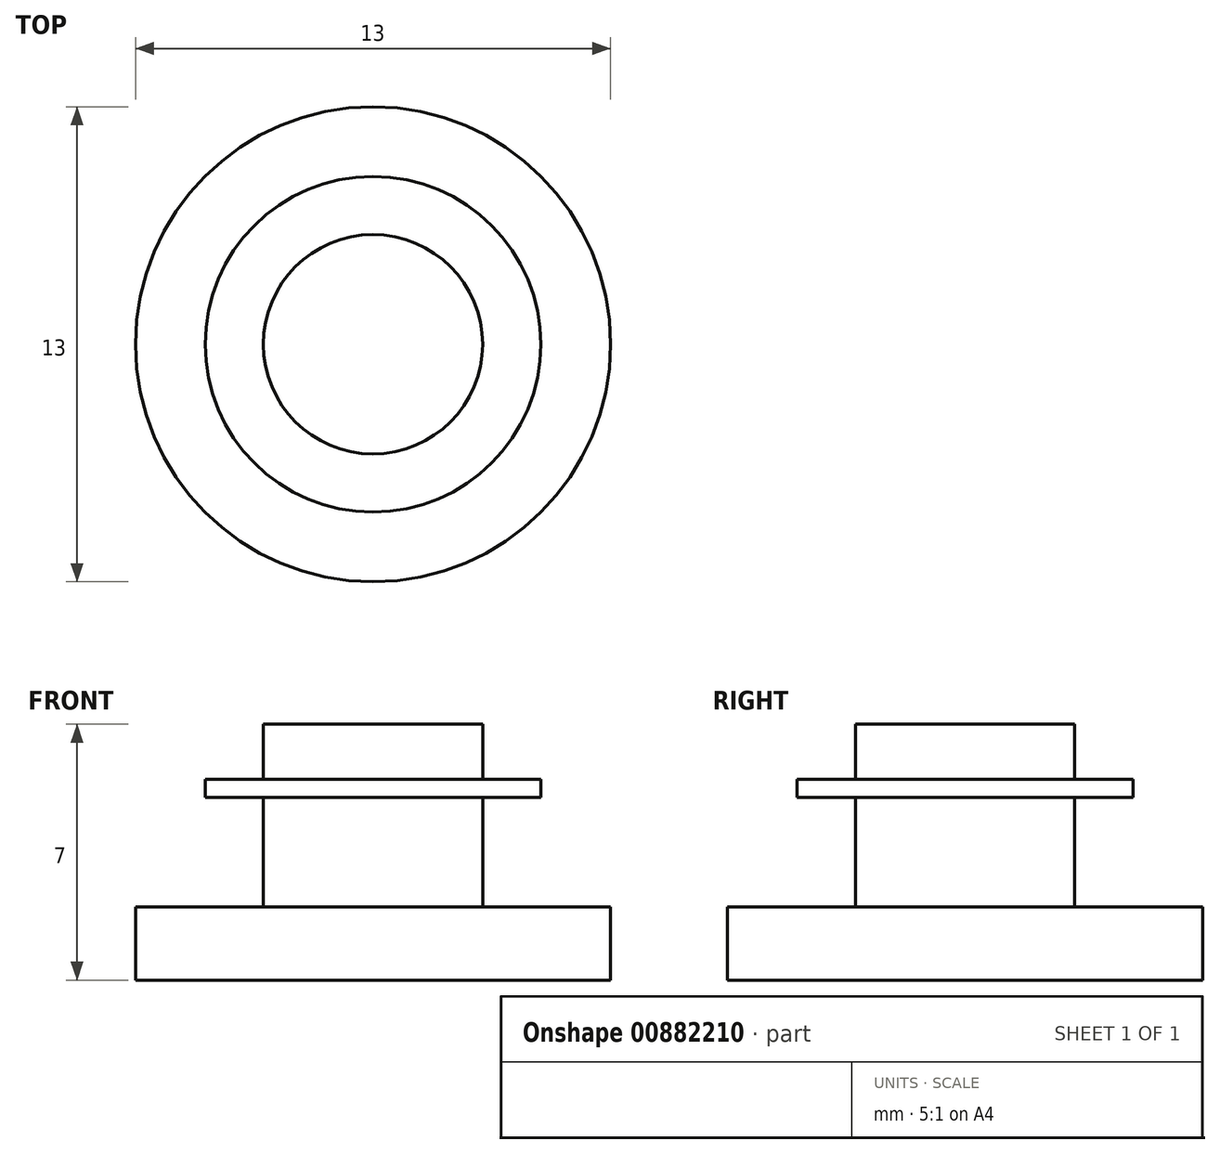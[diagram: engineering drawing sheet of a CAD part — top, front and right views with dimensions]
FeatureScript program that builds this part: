
annotation { "Feature Type Name" : "Feature", "Feature Type Description" : "" }
export const myFeature = defineFeature(function(context is Context, id is Id, definition is map)
    precondition{}
    {
        {
            var Q0;
            Q0=qCreatedBy(makeId("Top.planeOp"),FACE);
            var sketch = newSketch(context, id + "F0", { "sketchPlane" : qUnion([Q0])});
            skCircle(sketch, "E0", {"center": v(0, 0) * mm, "radius": 6.5 * mm});
            skSolve(sketch);
        }
        {
            var Q0;
            Q0 = qSketchRegion(id + "F0", true);
            extrude(context, id + "F1", {"entities" : qUnion([Q0]), "depth" : 2 * mm, "offsetDistance" : 25 * mm});
        }
        {
            var Q0;
            Q0=makeQuery(id+"F1.opExtrude","CAP_FACE",FACE,{"disambiguationData":[OSD([sQuery(id+"F0.wireOp",EDGE,"E0")])],"isStart":false});
            var sketch = newSketch(context, id + "F2", { "sketchPlane" : qUnion([Q0])});
            skCircle(sketch, "E1", {"center": v(0, 0) * mm, "radius": 3 * mm});
            skSolve(sketch);
        }
        {
            var Q0;
            Q0 = qSketchRegion(id + "F2", true);
            extrude(context, id + "F3", {"entities" : qUnion([Q0]), "operationType" : NewBodyOperationType.ADD, "depth" : 5 * mm, "offsetDistance" : 25 * mm});
        }
        {
            var Q0;
            Q0=qCreatedBy(makeId("Top.planeOp"),FACE);
            cPlane(context, id + "F4", {"entities" : qUnion([Q0]), "cplaneType" : CPlaneType.OFFSET, "offset" : 5 * mm, "width" : 150 * mm, "height" : 150 * mm});
        }
        {
            var Q0;
            Q0=qCreatedBy(id+"F4.planeOp",FACE);
            var sketch = newSketch(context, id + "F5", { "sketchPlane" : qUnion([Q0])});
            skCircle(sketch, "E2", {"center": v(0, 0) * mm, "radius": 4.6 * mm});
            skSolve(sketch);
        }
        {
            var Q0;
            Q0 = qSketchRegion(id + "F5", true);
            extrude(context, id + "F6", {"entities" : qUnion([Q0]), "operationType" : NewBodyOperationType.ADD, "depth" : .5 * mm, "offsetDistance" : 25 * mm});
        }
    });
